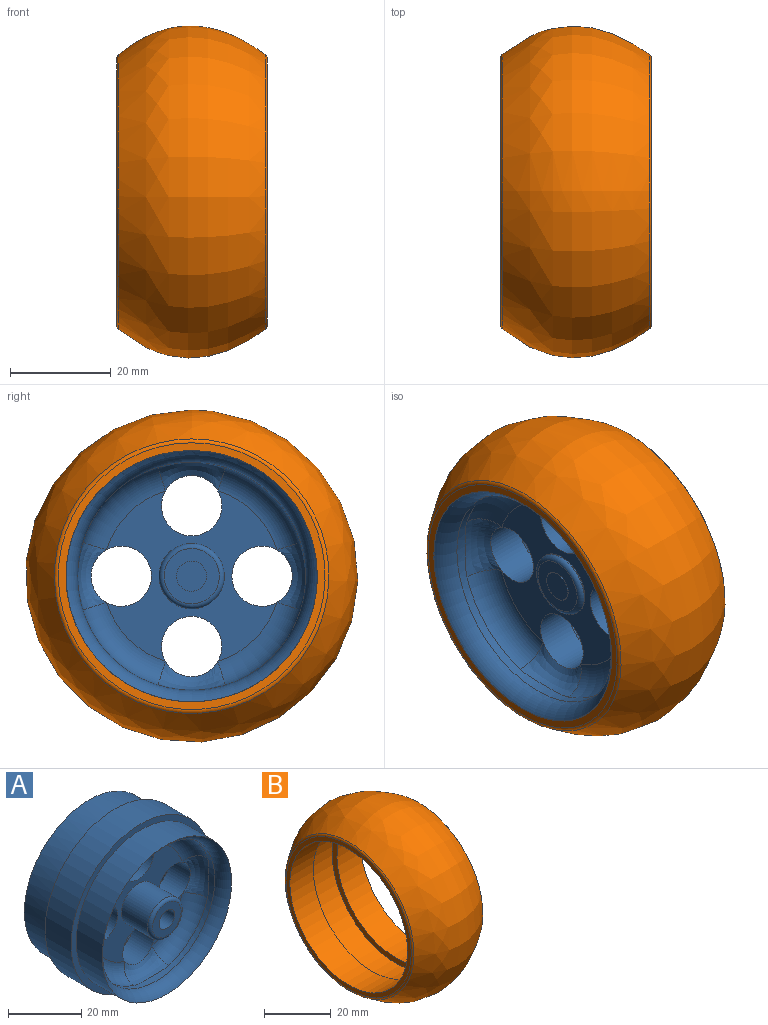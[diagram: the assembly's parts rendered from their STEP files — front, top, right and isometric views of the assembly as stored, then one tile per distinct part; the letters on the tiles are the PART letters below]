
ASSEMBLY  parts=2 mates=1
PART A: 41 faces, bbox 60x31.6x60 mm
  f0: cylinder r=6.51mm len=13.01mm, axis (0,1,0), area 8.2mm2, adj f16,f39
  f1: cylinder r=3mm len=15mm, axis (0,1,0), area 282.7mm2, adj f3,f35
  f2: cylinder r=6.51mm len=13.01mm, axis (0,1,0), area 408.8mm2, adj f15,f40
  f3: plane 11.01x11.01mm, normal (0,-1,0), area 67mm2, adj f1,f40
  f4: cylinder r=22.72mm len=45.45mm, axis (0,1,0), area 272.6mm2, adj f25,f26,f27,f28,f29,f30,f31,f32
  f5: cylinder r=25mm len=50mm, axis (0,1,0), area 1570.8mm2, adj f10,f33
  f6: cylinder r=22.72mm len=45.45mm, axis (0,1,0), area 272.5mm2, adj f17,f18,f19,f20,f21,f22,f23,f24
  f7: cylinder r=25mm len=50mm, axis (0,1,0), area 1570.8mm2, adj f9,f34
  f8: cylinder r=27mm len=54mm, axis (0,1,0), area 1696.5mm2, adj f9,f10
  f9: plane 54x54mm, normal (0,-1,0), area 326.7mm2, adj f7,f8
  f10: plane 54x54mm, normal (0,1,0), area 326.7mm2, adj f5,f8
  f11: cylinder r=6mm len=12mm, axis (0,1,0), area 301.6mm2, adj f15,f16,f21,f29
  f12: cylinder r=6mm len=12mm, axis (0,1,0), area 301.6mm2, adj f15,f16,f17,f25
  f13: cylinder r=6mm len=12mm, axis (0,1,0), area 301.6mm2, adj f15,f16,f20,f28
  f14: cylinder r=6mm len=12mm, axis (0,1,0), area 301.6mm2, adj f15,f16,f24,f32
  f15: plane 33.86x33.86mm, normal (0,-1,0), area 470.5mm2, adj f2,f11,f12,f13,f14,f18,f19,f22
  f16: plane 33.86x33.86mm, normal (0,1,0), area 470.5mm2, adj f0,f11,f12,f13,f14,f26,f27,f30
  f17: bspline ~14.08x5.97mm, area 81.2mm2, adj f6,f12,f18,f19
  f18: torus R=17.72mm, axis (0,-1,0), area 159.5mm2, adj f6,f15,f17,f20
  f19: torus R=17.72mm, axis (0,-1,0), area 159.5mm2, adj f6,f15,f17,f21
  f20: bspline ~14.08x5.97mm, area 81.2mm2, adj f6,f13,f18,f22
  f21: bspline ~14.08x5.97mm, area 81.2mm2, adj f6,f11,f19,f23
  f22: torus R=17.72mm, axis (0,-1,0), area 159.5mm2, adj f6,f15,f20,f24
  f23: torus R=17.72mm, axis (0,-1,0), area 159.5mm2, adj f6,f15,f21,f24
  f24: bspline ~14.08x5.97mm, area 81.2mm2, adj f6,f14,f22,f23
  f25: bspline ~15.07x6.43mm, area 81.1mm2, adj f4,f12,f26,f27
  f26: torus R=17.72mm, axis (0,-1,0), area 159.5mm2, adj f4,f16,f25,f28
  f27: torus R=17.72mm, axis (0,-1,0), area 159.5mm2, adj f4,f16,f25,f29
  f28: bspline ~15.07x6.43mm, area 81.1mm2, adj f4,f13,f26,f30
  f29: bspline ~15.07x6.43mm, area 81.1mm2, adj f4,f11,f27,f31
  f30: torus R=17.72mm, axis (0,-1,0), area 159.5mm2, adj f4,f16,f28,f32
  f31: torus R=17.72mm, axis (0,-1,0), area 159.5mm2, adj f4,f16,f29,f32
  f32: bspline ~15.07x6.43mm, area 81.1mm2, adj f4,f14,f30,f31
  f33: torus R=27.72mm, axis (0,1,0), area 734.7mm2, adj f4,f5
  f34: torus R=27.72mm, axis (0,-1,0), area 734.7mm2, adj f6,f7
  f35: plane 6x6mm, normal (0,-1,0), area 28.3mm2, adj f1
  f36: plane 11.01x11.01mm, normal (0,1,0), area 67mm2, adj f37,f39
  f37: cylinder r=3mm len=6mm, axis (0,-1,0), area 1.9mm2, adj f36,f38
  f38: plane 6x6mm, normal (0,1,0), area 28.3mm2, adj f37
  f39: torus R=5.51mm, axis (0,-1,0), area 60.6mm2, adj f0,f36
  f40: torus R=5.51mm, axis (0,-1,0), area 60.6mm2, adj f2,f3
PART B: 10 faces, bbox 30x66.1x66.1 mm
  f0: cylinder r=27mm len=54mm, axis (-1,0,0), area 1696.5mm2, adj f1,f5
  f1: plane 54x54mm, normal (1,0,0), area 326.7mm2, adj f0,f2
  f2: cylinder r=25mm len=50mm, axis (-1,0,0), area 1570.8mm2, adj f1,f3
  f3: plane 53.01x53.01mm, normal (-1,0,0), area 243.2mm2, adj f2,f4
  f4: torus R=26.5mm, axis (-1,0,0), area 157mm2, adj f3
  f5: plane 54x54mm, normal (-1,0,0), area 326.7mm2, adj f0,f6
  f6: cylinder r=25mm len=50mm, axis (-1,0,0), area 1570.8mm2, adj f5,f7
  f7: plane 53.07x53.07mm, normal (1,0,0), area 248.4mm2, adj f6,f8
  f8: torus R=26.53mm, axis (-1,0,0), area 148.7mm2, adj f7
  f9: revolved ~66.12x66.12mm, area 12480.9mm2
PLACE A rot(axis=(-0.58,0.58,0.58),120deg) t=(-29.93,-5.54,8.95)mm
PLACE B t=(-29.93,-5.54,8.95)mm
MATE fastened B.f0 <-> A.f5  axis (1,0,0) through (-34.93,-5.54,8.95)mm
